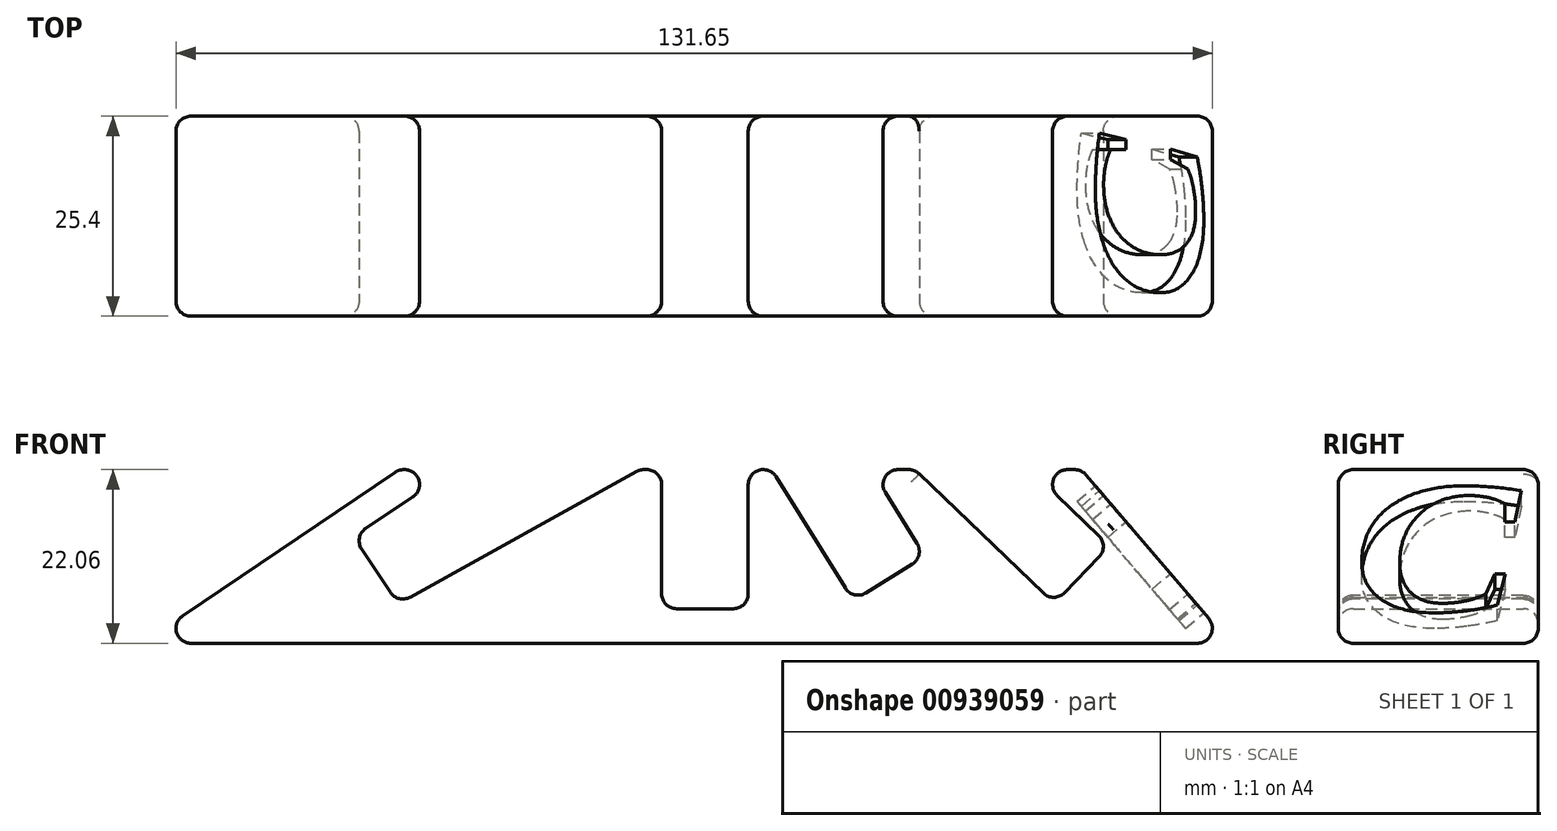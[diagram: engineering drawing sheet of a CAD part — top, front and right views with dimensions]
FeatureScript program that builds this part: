
annotation { "Feature Type Name" : "Feature", "Feature Type Description" : "" }
export const myFeature = defineFeature(function(context is Context, id is Id, definition is map)
    precondition{}
    {
        {
            var Q0;
            Q0=qCreatedBy(makeId("Front.planeOp"),FACE);
            var sketch = newSketch(context, id + "F0", { "sketchPlane" : qUnion([Q0])});
            skLineSegment(sketch, "E0", {"start": v(46.32, 11) * mm, "end": v(49.83, 11) * mm});
            skLineSegment(sketch, "E1", {"start": v(49.83, 11) * mm, "end": v(68.66, -11.06) * mm});
            skLineSegment(sketch, "E2", {"start": v(68.66, -11.06) * mm, "end": v(-69.51, -11.06) * mm});
            skLineSegment(sketch, "E3", {"start": v(-69.51, -11.06) * mm, "end": v(-36.88, 11) * mm});
            skLineSegment(sketch, "E4", {"start": v(-36.88, 11) * mm, "end": v(-29.87, 11) * mm});
            skLineSegment(sketch, "E5", {"start": v(-29.87, 11) * mm, "end": v(-42.68, 2.5) * mm});
            skLineSegment(sketch, "E6", {"start": v(-42.68, 2.5) * mm, "end": v(-37, -6.05) * mm});
            skLineSegment(sketch, "E7", {"start": v(-37, -6.05) * mm, "end": v(-6.27, 11) * mm});
            skLineSegment(sketch, "E8", {"start": v(-6.27, 11) * mm, "end": v(-3.51, 11) * mm});
            skLineSegment(sketch, "E9", {"start": v(-3.51, 11) * mm, "end": v(-3.51, -6.67) * mm});
            skLineSegment(sketch, "E10", {"start": v(-3.51, -6.67) * mm, "end": v(7.49, -6.67) * mm});
            skLineSegment(sketch, "E11", {"start": v(7.49, -6.67) * mm, "end": v(7.49, 11) * mm});
            skLineSegment(sketch, "E12", {"start": v(7.49, 11) * mm, "end": v(10.46, 11) * mm});
            skLineSegment(sketch, "E13", {"start": v(10.46, 11) * mm, "end": v(20.82, -5.67) * mm});
            skLineSegment(sketch, "E14", {"start": v(20.82, -5.67) * mm, "end": v(29.93, 0) * mm});
            skLineSegment(sketch, "E15", {"start": v(29.93, 0) * mm, "end": v(23.1, 11) * mm});
            skLineSegment(sketch, "E16", {"start": v(23.1, 11) * mm, "end": v(28.65, 11) * mm});
            skLineSegment(sketch, "E17", {"start": v(46.32, -6) * mm, "end": v(53.38, 1.29) * mm});
            skLineSegment(sketch, "E18", {"start": v(53.38, 1.29) * mm, "end": v(43.36, 11) * mm});
            skLineSegment(sketch, "E19", {"start": v(43.36, 11) * mm, "end": v(46.32, 11) * mm});
            skLineSegment(sketch, "E20", {"start": v(46.32, -6) * mm, "end": v(28.65, 11) * mm});
            skSolve(sketch);
        }
        {
            var Q0;
            Q0 = qSketchRegion(id + "F0", true);
            extrude(context, id + "F1", {"entities" : qUnion([Q0]), "endBound" : BoundingType.SYMMETRIC, "depth" : 25.4 * mm, "offsetDistance" : 25.4 * mm});
        }
        {
            var Q0;
            Q0=makeQuery(id+"F1.opExtrude","CAP_EDGE",EDGE,{"disambiguationData":[OSD([sQuery(id+"F0.wireOp",EDGE,"E14")])],"isStart":true});
            var Q1;
            Q1=makeQuery(id+"F1.opExtrude","CAP_EDGE",EDGE,{"disambiguationData":[OSD([sQuery(id+"F0.wireOp",EDGE,"E6")])],"isStart":true});
            var Q2;
            Q2=makeQuery(id+"F1.opExtrude","CAP_EDGE",EDGE,{"disambiguationData":[OSD([sQuery(id+"F0.wireOp",EDGE,"E3")])],"isStart":true});
            var Q3;
            Q3=makeQuery(id+"F1.opExtrude","CAP_EDGE",EDGE,{"disambiguationData":[OSD([sQuery(id+"F0.wireOp",EDGE,"E13")])],"isStart":true});
            var Q4;
            Q4=makeQuery(id+"F1.opExtrude","CAP_EDGE",EDGE,{"disambiguationData":[OSD([sQuery(id+"F0.wireOp",EDGE,"E20")])],"isStart":true});
            var Q5;
            Q5=makeQuery(id+"F1.opExtrude","CAP_EDGE",EDGE,{"disambiguationData":[OSD([sQuery(id+"F0.wireOp",EDGE,"E7")])],"isStart":true});
            var Q6;
            Q6=makeQuery(id+"F1.opExtrude","CAP_EDGE",EDGE,{"disambiguationData":[OSD([sQuery(id+"F0.wireOp",EDGE,"E1")])],"isStart":true});
            var Q7;
            Q7=makeQuery(id+"F1.opExtrude","CAP_EDGE",EDGE,{"disambiguationData":[OSD([sQuery(id+"F0.wireOp",EDGE,"E18")])],"isStart":true});
            var Q8;
            Q8=makeQuery(id+"F1.opExtrude","CAP_EDGE",EDGE,{"disambiguationData":[OSD([sQuery(id+"F0.wireOp",EDGE,"E17")])],"isStart":true});
            var Q9;
            Q9=makeQuery(id+"F1.opExtrude","CAP_EDGE",EDGE,{"disambiguationData":[OSD([sQuery(id+"F0.wireOp",EDGE,"E15")])],"isStart":true});
            var Q10;
            Q10=makeQuery(id+"F1.opExtrude","CAP_EDGE",EDGE,{"disambiguationData":[OSD([sQuery(id+"F0.wireOp",EDGE,"E5")])],"isStart":true});
            var Q11;
            Q11=makeQuery(id+"F1.opExtrude","SWEPT_EDGE",EDGE,{"disambiguationData":[OSD([sQuery(id+"F0.wireOp",EDGE,"E0"),sQuery(id+"F0.wireOp",EDGE,"E1")])]});
            var Q12;
            Q12=makeQuery(id+"F1.opExtrude","CAP_EDGE",EDGE,{"disambiguationData":[OSD([sQuery(id+"F0.wireOp",EDGE,"E14")])],"isStart":false});
            var Q13;
            Q13=makeQuery(id+"F1.opExtrude","CAP_EDGE",EDGE,{"disambiguationData":[OSD([sQuery(id+"F0.wireOp",EDGE,"E7")])],"isStart":false});
            var Q14;
            Q14=makeQuery(id+"F1.opExtrude","SWEPT_EDGE",EDGE,{"disambiguationData":[OSD([sQuery(id+"F0.wireOp",EDGE,"E17"),sQuery(id+"F0.wireOp",EDGE,"E18")])]});
            var Q15;
            Q15=makeQuery(id+"F1.opExtrude","SWEPT_EDGE",EDGE,{"disambiguationData":[OSD([sQuery(id+"F0.wireOp",EDGE,"E5"),sQuery(id+"F0.wireOp",EDGE,"E6")])]});
            var Q16;
            Q16=makeQuery(id+"F1.opExtrude","SWEPT_EDGE",EDGE,{"disambiguationData":[OSD([sQuery(id+"F0.wireOp",EDGE,"E13"),sQuery(id+"F0.wireOp",EDGE,"E14")])]});
            var Q17;
            Q17=makeQuery(id+"F1.opExtrude","SWEPT_EDGE",EDGE,{"disambiguationData":[OSD([sQuery(id+"F0.wireOp",EDGE,"E17"),sQuery(id+"F0.wireOp",EDGE,"E20")])]});
            var Q18;
            Q18=makeQuery(id+"F1.opExtrude","CAP_EDGE",EDGE,{"disambiguationData":[OSD([sQuery(id+"F0.wireOp",EDGE,"E13")])],"isStart":false});
            var Q19;
            Q19=makeQuery(id+"F1.opExtrude","CAP_EDGE",EDGE,{"disambiguationData":[OSD([sQuery(id+"F0.wireOp",EDGE,"E11")])],"isStart":true});
            var Q20;
            Q20=makeQuery(id+"F1.opExtrude","CAP_EDGE",EDGE,{"disambiguationData":[OSD([sQuery(id+"F0.wireOp",EDGE,"E6")])],"isStart":false});
            var Q21;
            Q21=makeQuery(id+"F1.opExtrude","CAP_EDGE",EDGE,{"disambiguationData":[OSD([sQuery(id+"F0.wireOp",EDGE,"E15")])],"isStart":false});
            var Q22;
            Q22=makeQuery(id+"F1.opExtrude","CAP_EDGE",EDGE,{"disambiguationData":[OSD([sQuery(id+"F0.wireOp",EDGE,"E18")])],"isStart":false});
            var Q23;
            Q23=makeQuery(id+"F1.opExtrude","CAP_EDGE",EDGE,{"disambiguationData":[OSD([sQuery(id+"F0.wireOp",EDGE,"E4")])],"isStart":true});
            var Q24;
            Q24=makeQuery(id+"F1.opExtrude","CAP_EDGE",EDGE,{"disambiguationData":[OSD([sQuery(id+"F0.wireOp",EDGE,"E1")])],"isStart":false});
            var Q25;
            Q25=makeQuery(id+"F1.opExtrude","CAP_EDGE",EDGE,{"disambiguationData":[OSD([sQuery(id+"F0.wireOp",EDGE,"E16")])],"isStart":true});
            var Q26;
            Q26=makeQuery(id+"F1.opExtrude","CAP_EDGE",EDGE,{"disambiguationData":[OSD([sQuery(id+"F0.wireOp",EDGE,"E17")])],"isStart":false});
            var Q27;
            Q27=makeQuery(id+"F1.opExtrude","CAP_EDGE",EDGE,{"disambiguationData":[OSD([sQuery(id+"F0.wireOp",EDGE,"E20")])],"isStart":false});
            var Q28;
            Q28=makeQuery(id+"F1.opExtrude","SWEPT_EDGE",EDGE,{"disambiguationData":[OSD([sQuery(id+"F0.wireOp",EDGE,"E14"),sQuery(id+"F0.wireOp",EDGE,"E15")])]});
            var Q29;
            Q29=makeQuery(id+"F1.opExtrude","CAP_EDGE",EDGE,{"disambiguationData":[OSD([sQuery(id+"F0.wireOp",EDGE,"E12")])],"isStart":true});
            var Q30;
            Q30=makeQuery(id+"F1.opExtrude","CAP_EDGE",EDGE,{"disambiguationData":[OSD([sQuery(id+"F0.wireOp",EDGE,"E5")])],"isStart":false});
            var Q31;
            Q31=makeQuery(id+"F1.opExtrude","SWEPT_EDGE",EDGE,{"disambiguationData":[OSD([sQuery(id+"F0.wireOp",EDGE,"E2"),sQuery(id+"F0.wireOp",EDGE,"E3")])]});
            var Q32;
            Q32=makeQuery(id+"F1.opExtrude","SWEPT_EDGE",EDGE,{"disambiguationData":[OSD([sQuery(id+"F0.wireOp",EDGE,"E1"),sQuery(id+"F0.wireOp",EDGE,"E2")])]});
            var Q33;
            Q33=makeQuery(id+"F1.opExtrude","CAP_EDGE",EDGE,{"disambiguationData":[OSD([sQuery(id+"F0.wireOp",EDGE,"E3")])],"isStart":false});
            var Q34;
            Q34=makeQuery(id+"F1.opExtrude","CAP_EDGE",EDGE,{"disambiguationData":[OSD([sQuery(id+"F0.wireOp",EDGE,"E0"),sQuery(id+"F0.wireOp",EDGE,"E19")])],"isStart":true});
            var Q35;
            Q35=makeQuery(id+"F1.opExtrude","SWEPT_EDGE",EDGE,{"disambiguationData":[OSD([sQuery(id+"F0.wireOp",EDGE,"E18"),sQuery(id+"F0.wireOp",EDGE,"E19")])]});
            var Q36;
            Q36=makeQuery(id+"F1.opExtrude","CAP_EDGE",EDGE,{"disambiguationData":[OSD([sQuery(id+"F0.wireOp",EDGE,"E8")])],"isStart":true});
            var Q37;
            Q37=makeQuery(id+"F1.opExtrude","SWEPT_EDGE",EDGE,{"disambiguationData":[OSD([sQuery(id+"F0.wireOp",EDGE,"E3"),sQuery(id+"F0.wireOp",EDGE,"E4")])]});
            var Q38;
            Q38=makeQuery(id+"F1.opExtrude","SWEPT_EDGE",EDGE,{"disambiguationData":[OSD([sQuery(id+"F0.wireOp",EDGE,"E6"),sQuery(id+"F0.wireOp",EDGE,"E7")])]});
            var Q39;
            Q39=makeQuery(id+"F1.opExtrude","SWEPT_EDGE",EDGE,{"disambiguationData":[OSD([sQuery(id+"F0.wireOp",EDGE,"E11"),sQuery(id+"F0.wireOp",EDGE,"E12")])]});
            var Q40;
            Q40=makeQuery(id+"F1.opExtrude","CAP_EDGE",EDGE,{"disambiguationData":[OSD([sQuery(id+"F0.wireOp",EDGE,"E9")])],"isStart":true});
            var Q41;
            Q41=makeQuery(id+"F1.opExtrude","SWEPT_EDGE",EDGE,{"disambiguationData":[OSD([sQuery(id+"F0.wireOp",EDGE,"E10"),sQuery(id+"F0.wireOp",EDGE,"E11")])]});
            var Q42;
            Q42=makeQuery(id+"F1.opExtrude","CAP_EDGE",EDGE,{"disambiguationData":[OSD([sQuery(id+"F0.wireOp",EDGE,"E10")])],"isStart":true});
            var Q43;
            Q43=makeQuery(id+"F1.opExtrude","CAP_EDGE",EDGE,{"disambiguationData":[OSD([sQuery(id+"F0.wireOp",EDGE,"E12")])],"isStart":false});
            var Q44;
            Q44=makeQuery(id+"F1.opExtrude","SWEPT_EDGE",EDGE,{"disambiguationData":[OSD([sQuery(id+"F0.wireOp",EDGE,"E16"),sQuery(id+"F0.wireOp",EDGE,"E20")])]});
            var Q45;
            Q45=makeQuery(id+"F1.opExtrude","SWEPT_EDGE",EDGE,{"disambiguationData":[OSD([sQuery(id+"F0.wireOp",EDGE,"E4"),sQuery(id+"F0.wireOp",EDGE,"E5")])]});
            var Q46;
            Q46=makeQuery(id+"F1.opExtrude","SWEPT_EDGE",EDGE,{"disambiguationData":[OSD([sQuery(id+"F0.wireOp",EDGE,"E12"),sQuery(id+"F0.wireOp",EDGE,"E13")])]});
            var Q47;
            Q47=makeQuery(id+"F1.opExtrude","SWEPT_EDGE",EDGE,{"disambiguationData":[OSD([sQuery(id+"F0.wireOp",EDGE,"E7"),sQuery(id+"F0.wireOp",EDGE,"E8")])]});
            var Q48;
            Q48=makeQuery(id+"F1.opExtrude","CAP_EDGE",EDGE,{"disambiguationData":[OSD([sQuery(id+"F0.wireOp",EDGE,"E2")])],"isStart":true});
            var Q49;
            Q49=makeQuery(id+"F1.opExtrude","CAP_EDGE",EDGE,{"disambiguationData":[OSD([sQuery(id+"F0.wireOp",EDGE,"E11")])],"isStart":false});
            var Q50;
            Q50=makeQuery(id+"F1.opExtrude","CAP_EDGE",EDGE,{"disambiguationData":[OSD([sQuery(id+"F0.wireOp",EDGE,"E16")])],"isStart":false});
            var Q51;
            Q51=makeQuery(id+"F1.opExtrude","CAP_EDGE",EDGE,{"disambiguationData":[OSD([sQuery(id+"F0.wireOp",EDGE,"E4")])],"isStart":false});
            var Q52;
            Q52=makeQuery(id+"F1.opExtrude","SWEPT_EDGE",EDGE,{"disambiguationData":[OSD([sQuery(id+"F0.wireOp",EDGE,"E15"),sQuery(id+"F0.wireOp",EDGE,"E16")])]});
            var Q53;
            Q53=makeQuery(id+"F1.opExtrude","CAP_EDGE",EDGE,{"disambiguationData":[OSD([sQuery(id+"F0.wireOp",EDGE,"E0"),sQuery(id+"F0.wireOp",EDGE,"E19")])],"isStart":false});
            var Q54;
            Q54=makeQuery(id+"F1.opExtrude","SWEPT_EDGE",EDGE,{"disambiguationData":[OSD([sQuery(id+"F0.wireOp",EDGE,"E8"),sQuery(id+"F0.wireOp",EDGE,"E9")])]});
            var Q55;
            Q55=makeQuery(id+"F1.opExtrude","CAP_EDGE",EDGE,{"disambiguationData":[OSD([sQuery(id+"F0.wireOp",EDGE,"E8")])],"isStart":false});
            var Q56;
            Q56=makeQuery(id+"F1.opExtrude","CAP_EDGE",EDGE,{"disambiguationData":[OSD([sQuery(id+"F0.wireOp",EDGE,"E9")])],"isStart":false});
            var Q57;
            Q57=makeQuery(id+"F1.opExtrude","CAP_EDGE",EDGE,{"disambiguationData":[OSD([sQuery(id+"F0.wireOp",EDGE,"E10")])],"isStart":false});
            var Q58;
            Q58=makeQuery(id+"F1.opExtrude","CAP_EDGE",EDGE,{"disambiguationData":[OSD([sQuery(id+"F0.wireOp",EDGE,"E2")])],"isStart":false});
            var Q59;
            Q59=makeQuery(id+"F1.opExtrude","SWEPT_EDGE",EDGE,{"disambiguationData":[OSD([sQuery(id+"F0.wireOp",EDGE,"E9"),sQuery(id+"F0.wireOp",EDGE,"E10")])]});
            var Q60;
            Q60=makeQuery(id+"F1.opExtrude","SWEPT_FACE",FACE,{"disambiguationData":[OSD([sQuery(id+"F0.wireOp",EDGE,"E3")])]});
            var Q61;
            Q61=makeQuery(id+"F1.opExtrude","CAP_FACE",FACE,{"disambiguationData":[OSD([sQuery(id+"F0.wireOp",EDGE,"E0"),sQuery(id+"F0.wireOp",EDGE,"E1"),sQuery(id+"F0.wireOp",EDGE,"E2"),sQuery(id+"F0.wireOp",EDGE,"E3"),sQuery(id+"F0.wireOp",EDGE,"E4"),sQuery(id+"F0.wireOp",EDGE,"E5"),sQuery(id+"F0.wireOp",EDGE,"E6"),sQuery(id+"F0.wireOp",EDGE,"E7"),sQuery(id+"F0.wireOp",EDGE,"E8"),sQuery(id+"F0.wireOp",EDGE,"E9"),sQuery(id+"F0.wireOp",EDGE,"E10"),sQuery(id+"F0.wireOp",EDGE,"E11"),sQuery(id+"F0.wireOp",EDGE,"E12"),sQuery(id+"F0.wireOp",EDGE,"E13"),sQuery(id+"F0.wireOp",EDGE,"E14"),sQuery(id+"F0.wireOp",EDGE,"E15"),sQuery(id+"F0.wireOp",EDGE,"E16"),sQuery(id+"F0.wireOp",EDGE,"E17"),sQuery(id+"F0.wireOp",EDGE,"E18"),sQuery(id+"F0.wireOp",EDGE,"E19"),sQuery(id+"F0.wireOp",EDGE,"E20")])],"isStart":false});
            fillet(context, id + "F2", {"entities" : qUnion([Q0, Q1, Q2, Q3, Q4, Q5, Q6, Q7, Q8, Q9, Q10, Q11, Q12, Q13, Q14, Q15, Q16, Q17, Q18, Q19, Q20, Q21, Q22, Q23, Q24, Q25, Q26, Q27, Q28, Q29, Q30, Q31, Q32, Q33, Q34, Q35, Q36, Q37, Q38, Q39, Q40, Q41, Q42, Q43, Q44, Q45, Q46, Q47, Q48, Q49, Q50, Q51, Q52, Q53, Q54, Q55, Q56, Q57, Q58, Q59, Q60, Q61]), "radius" : 1.9 * mm, "tangentPropagation" : true, "allowEdgeOverflow" : false});
        }
        {
            var Q0;
            Q0=makeQuery(id+"F1.opExtrude","SWEPT_FACE",FACE,{"disambiguationData":[OSD([sQuery(id+"F0.wireOp",EDGE,"E1")])]});
            var sketch = newSketch(context, id + "F3", { "sketchPlane" : qUnion([Q0])});
            skText(sketch, "E21", { "text": "C", "fontName": "Tinos-BoldItalic.ttf"});
            const initialGuessF3  = {"E21": [-0.0108, -0.04759, 1, 0, 0.02273]};
            skSetInitialGuess(sketch, initialGuessF3);
            skSolve(sketch);
        }
        {
            var Q0;
            Q0=makeQuery(id+"F3.imprint","IMPRINT",FACE,{"disambiguationData":[TD([[makeQuery(id+"F3.imprint","IMPRINT",EDGE,{"derivedFrom":sQuery(id+"F3.wireOp",EDGE,"E21.sketch_text.stroke-0")}),-1.0]])]});
            extrude(context, id + "F4", {"entities" : qUnion([Q0]), "operationType" : NewBodyOperationType.REMOVE, "oppositeDirection" : true, "depth" : 3.05 * mm, "offsetDistance" : 25.4 * mm});
        }
    });
